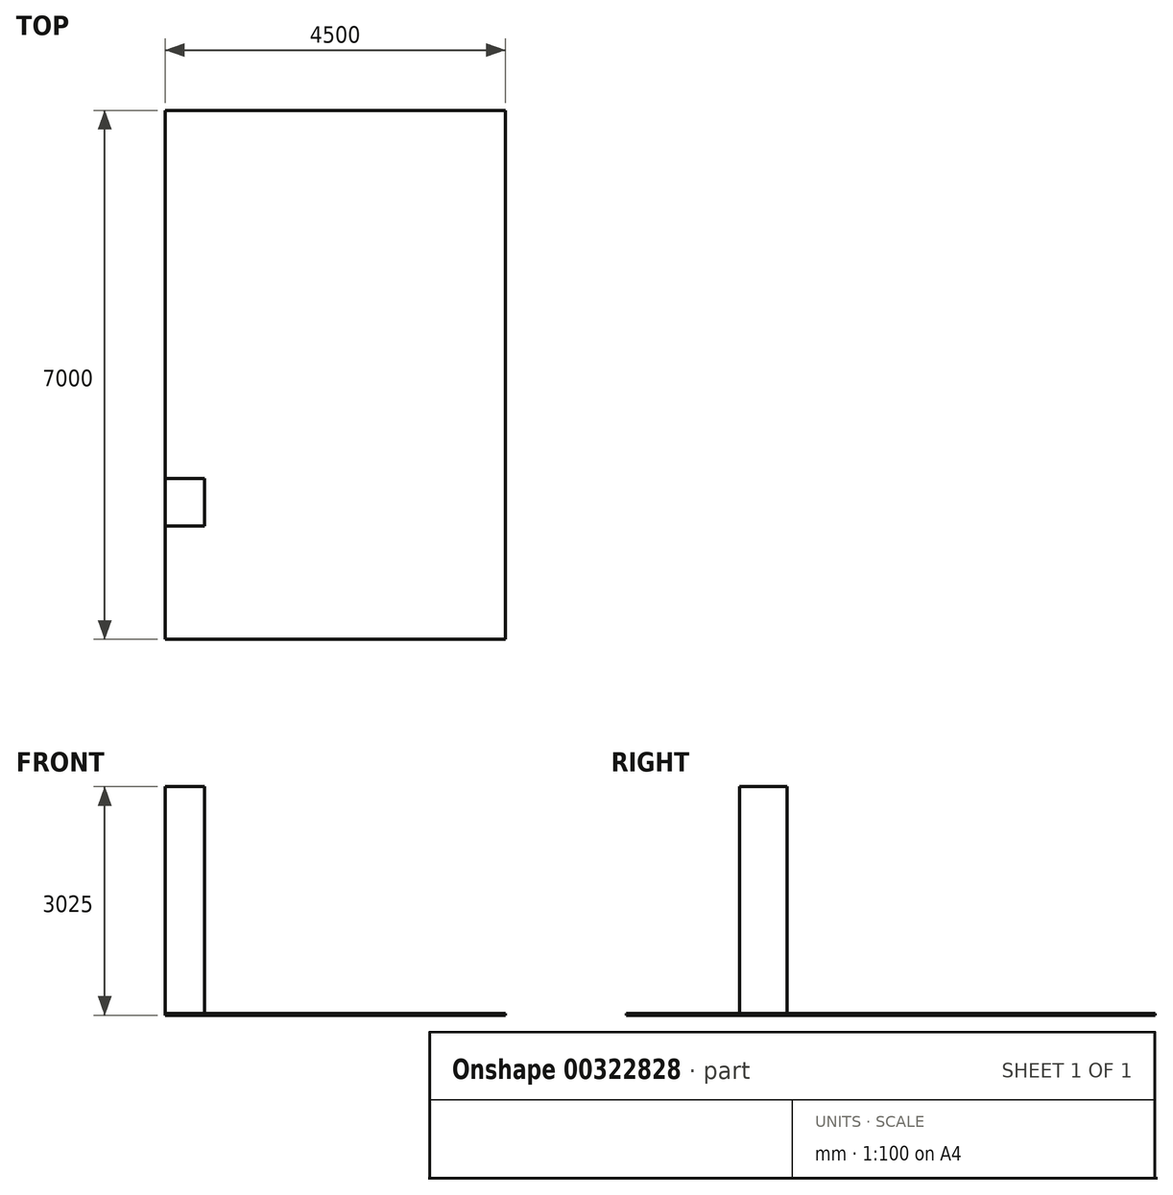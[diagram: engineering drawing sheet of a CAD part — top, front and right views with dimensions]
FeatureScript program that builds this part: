
annotation { "Feature Type Name" : "Feature", "Feature Type Description" : "" }
export const myFeature = defineFeature(function(context is Context, id is Id, definition is map)
    precondition{}
    {
        {
            var Q0;
            Q0=qCreatedBy(makeId("Top.planeOp"),FACE);
            var sketch = newSketch(context, id + "F0", { "sketchPlane" : qUnion([Q0])});
            skLineSegment(sketch, "E0.bottom", {"start": v(2250, -3500) * mm, "end": v(-2250, -3500) * mm});
            skLineSegment(sketch, "E0.top", {"start": v(2250, 3500) * mm, "end": v(-2250, 3500) * mm});
            skLineSegment(sketch, "E0.left", {"start": v(2250, -3500) * mm, "end": v(2250, 3500) * mm});
            skLineSegment(sketch, "E0.right", {"start": v(-2250, -3500) * mm, "end": v(-2250, 3500) * mm});
            skPoint(sketch, "E0.middle", {"position": v(0, 0) * mm});
            skLineSegment(sketch, "E1", {"start": v(-2250, -3500) * mm, "end": v(-2250, -2000) * mm});
            skLineSegment(sketch, "E2", {"start": v(-2250, -2000) * mm, "end": v(-1730, -2000) * mm});
            skLineSegment(sketch, "E3", {"start": v(-1730, -2000) * mm, "end": v(-1730, -1370) * mm});
            skLineSegment(sketch, "E4", {"start": v(-1730, -1370) * mm, "end": v(-2250, -1370) * mm});
            skLineSegment(sketch, "E5", {"start": v(-2250, -1370) * mm, "end": v(-2250, 3500) * mm});
            skLineSegment(sketch, "E6", {"start": v(-2250, -2000) * mm, "end": v(-2250, -3500) * mm});
            skSolve(sketch);
        }
        {
            var Q0;
            Q0=makeQuery(id+"F0.imprint","IMPRINT",FACE,{"disambiguationData":[TD([[makeQuery(id+"F0.imprint","IMPRINT",EDGE,{"derivedFrom":sQuery(id+"F0.wireOp",EDGE,"E0.bottom")}),-1.0]])]});
            extrude(context, id + "F1", {"entities" : qUnion([Q0]), "depth" : 25 * mm});
        }
        {
            var Q0;
            Q0=makeQuery(id+"F0.imprint","IMPRINT",FACE,{"disambiguationData":[TD([[makeQuery(id+"F0.imprint","IMPRINT",EDGE,{"derivedFrom":sQuery(id+"F0.wireOp",EDGE,"E0.right")}),-1.0]])]});
            extrude(context, id + "F2", {"entities" : qUnion([Q0]), "depth" : 3025 * mm});
        }
    });
